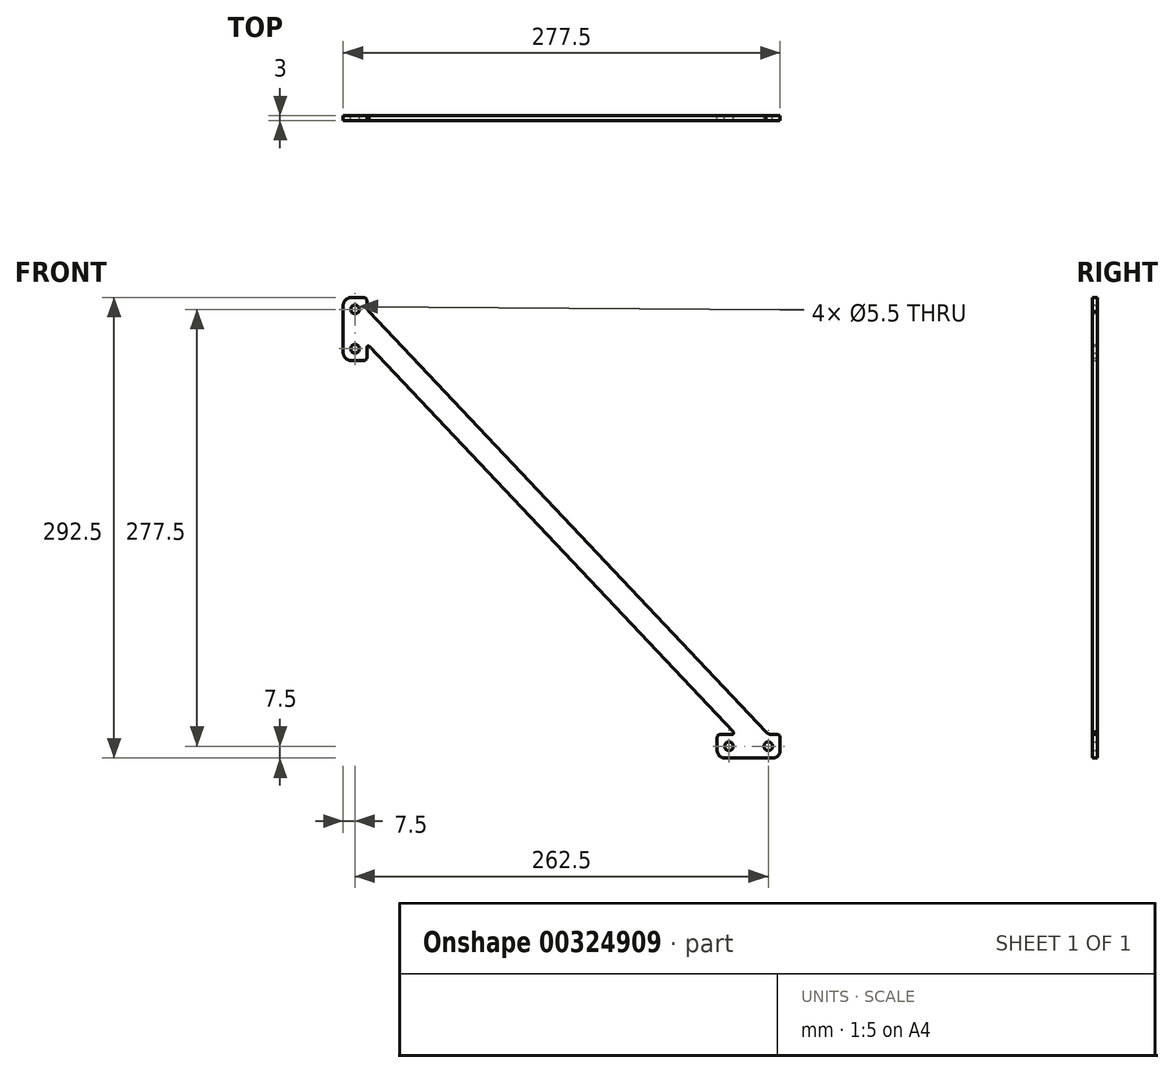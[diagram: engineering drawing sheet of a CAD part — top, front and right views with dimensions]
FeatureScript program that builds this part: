
annotation { "Feature Type Name" : "Feature", "Feature Type Description" : "" }
export const myFeature = defineFeature(function(context is Context, id is Id, definition is map)
    precondition{}
    {
        {
            var Q0;
            Q0=qCreatedBy(makeId("Front.planeOp"),FACE);
            var sketch = newSketch(context, id + "F0", { "sketchPlane" : qUnion([Q0])});
            skCircle(sketch, "E0", {"center": v(0, 0) * mm, "radius": 2.75 * mm});
            skCircle(sketch, "E1", {"center": v(25, 0) * mm, "radius": 2.75 * mm});
            skLineSegment(sketch, "E2.bottom", {"start": v(1.97, 7.5) * mm, "end": v(-5.5, 7.5) * mm});
            skLineSegment(sketch, "E2.top", {"start": v(27.5, -7.5) * mm, "end": v(-2.5, -7.5) * mm});
            skLineSegment(sketch, "E2.left", {"start": v(32.5, 5.5) * mm, "end": v(32.5, -2.5) * mm});
            skLineSegment(sketch, "E2.right", {"start": v(-7.5, 5.5) * mm, "end": v(-7.5, -2.5) * mm});
            skPoint(sketch, "E2.middle", {"position": v(12.5, 0) * mm});
            skPoint(sketch, "E3.visualSharp", {"position": v(-7.5, -7.5) * mm});
            skArc(sketch, "E3.filletArc", {"start": v(-7.5, -2.5) * mm, "mid": v(-6.04, -6.04) * mm, "end": v(-2.5, -7.5) * mm});
            skPoint(sketch, "E4.visualSharp", {"position": v(32.5, -7.5) * mm});
            skArc(sketch, "E4.filletArc", {"start": v(27.5, -7.5) * mm, "mid": v(31.04, -6.04) * mm, "end": v(32.5, -2.5) * mm});
            skPoint(sketch, "E5.newPointB", {"position": v(32.5, 7.5) * mm});
            skLineSegment(sketch, "E6", {"start": v(27.07, 7.5) * mm, "end": v(30.5, 7.5) * mm});
            skPoint(sketch, "E7.visualSharp", {"position": v(25, 7.5) * mm});
            skArc(sketch, "E7.filletArc", {"start": v(23.54, 8.96) * mm, "mid": v(25.16, 7.88) * mm, "end": v(27.07, 7.5) * mm});
            skLineSegment(sketch, "E8", {"start": v(12.5, 0) * mm, "end": v(-245, 0) * mm, "construction": true});
            skPoint(sketch, "E9.visualSharp", {"position": v(-7.5, 7.5) * mm});
            skArc(sketch, "E9.filletArc", {"start": v(-5.5, 7.5) * mm, "mid": v(-6.91, 6.91) * mm, "end": v(-7.5, 5.5) * mm});
            skArc(sketch, "E10.filletArc", {"start": v(32.5, 5.5) * mm, "mid": v(31.91, 6.91) * mm, "end": v(30.5, 7.5) * mm});
            skCircle(sketch, "E11", {"center": v(-237.5, 277.5) * mm, "radius": 2.75 * mm});
            skCircle(sketch, "E12", {"center": v(-237.5, 252.5) * mm, "radius": 2.75 * mm});
            skLineSegment(sketch, "E13.top", {"start": v(-245, 250) * mm, "end": v(-245, 280) * mm});
            skLineSegment(sketch, "E13.left", {"start": v(-231.96, 245) * mm, "end": v(-240, 245) * mm});
            skLineSegment(sketch, "E13.right", {"start": v(-232, 285) * mm, "end": v(-240, 285) * mm});
            skPoint(sketch, "E13.middle", {"position": v(-237.5, 265) * mm});
            skPoint(sketch, "E14.visualSharp", {"position": v(-245, 285) * mm});
            skArc(sketch, "E14.filletArc", {"start": v(-240, 285) * mm, "mid": v(-243.54, 283.54) * mm, "end": v(-245, 280) * mm});
            skPoint(sketch, "E15.visualSharp", {"position": v(-245, 245) * mm});
            skArc(sketch, "E15.filletArc", {"start": v(-245, 250) * mm, "mid": v(-243.54, 246.46) * mm, "end": v(-240, 245) * mm});
            skPoint(sketch, "E16.newPointA", {"position": v(-241.2, 277.48) * mm});
            skPoint(sketch, "E16.newPointB", {"position": v(-230, 245) * mm});
            skPoint(sketch, "E17.visualSharp", {"position": v(-230, 285) * mm});
            skArc(sketch, "E17.filletArc", {"start": v(-230, 283) * mm, "mid": v(-230.59, 284.41) * mm, "end": v(-232, 285) * mm});
            skArc(sketch, "E18.filletArc", {"start": v(-231.96, 245) * mm, "mid": v(-230.7, 245.45) * mm, "end": v(-230, 246.6) * mm});
            skLineSegment(sketch, "E19", {"start": v(-230, 246.6) * mm, "end": v(-230, 253.2) * mm});
            skArc(sketch, "E20.filletArc", {"start": v(-230.02, 279.57) * mm, "mid": v(-229.64, 277.66) * mm, "end": v(-228.56, 276.04) * mm});
            skLineSegment(sketch, "E21", {"start": v(-230.02, 279.57) * mm, "end": v(-230, 283) * mm});
            skLineSegment(sketch, "E22", {"start": v(-228.56, 276.04) * mm, "end": v(23.54, 8.96) * mm});
            skPoint(sketch, "E23.visualSharp", {"position": v(-230, 254.95) * mm});
            skLineSegment(sketch, "E24.0", {"start": v(-228.27, 253.88) * mm, "end": v(2.7, 9.19) * mm});
            skLineSegment(sketch, "E25.trimOffspring", {"start": v(11.37, 0) * mm, "end": v(12.63, -1.33) * mm});
            skPoint(sketch, "E26.visualSharp", {"position": v(-230, 255.71) * mm});
            skArc(sketch, "E26.filletArc", {"start": v(-228.27, 253.88) * mm, "mid": v(-229.37, 254.13) * mm, "end": v(-230, 253.2) * mm});
            skPoint(sketch, "E27.visualSharp", {"position": v(4.3, 7.5) * mm});
            skArc(sketch, "E27.filletArc", {"start": v(1.97, 7.5) * mm, "mid": v(2.9, 8.1) * mm, "end": v(2.7, 9.19) * mm});
            skSolve(sketch);
        }
        {
            var Q0;
            Q0=makeQuery(id+"F0.imprint","IMPRINT",FACE,{"disambiguationData":[TD([[makeQuery(id+"F0.imprint","IMPRINT",EDGE,{"derivedFrom":sQuery(id+"F0.wireOp",EDGE,"E0")}),-1.0]])]});
            extrude(context, id + "F1", {"entities" : qUnion([Q0]), "depth" : 3 * mm});
        }
    });
